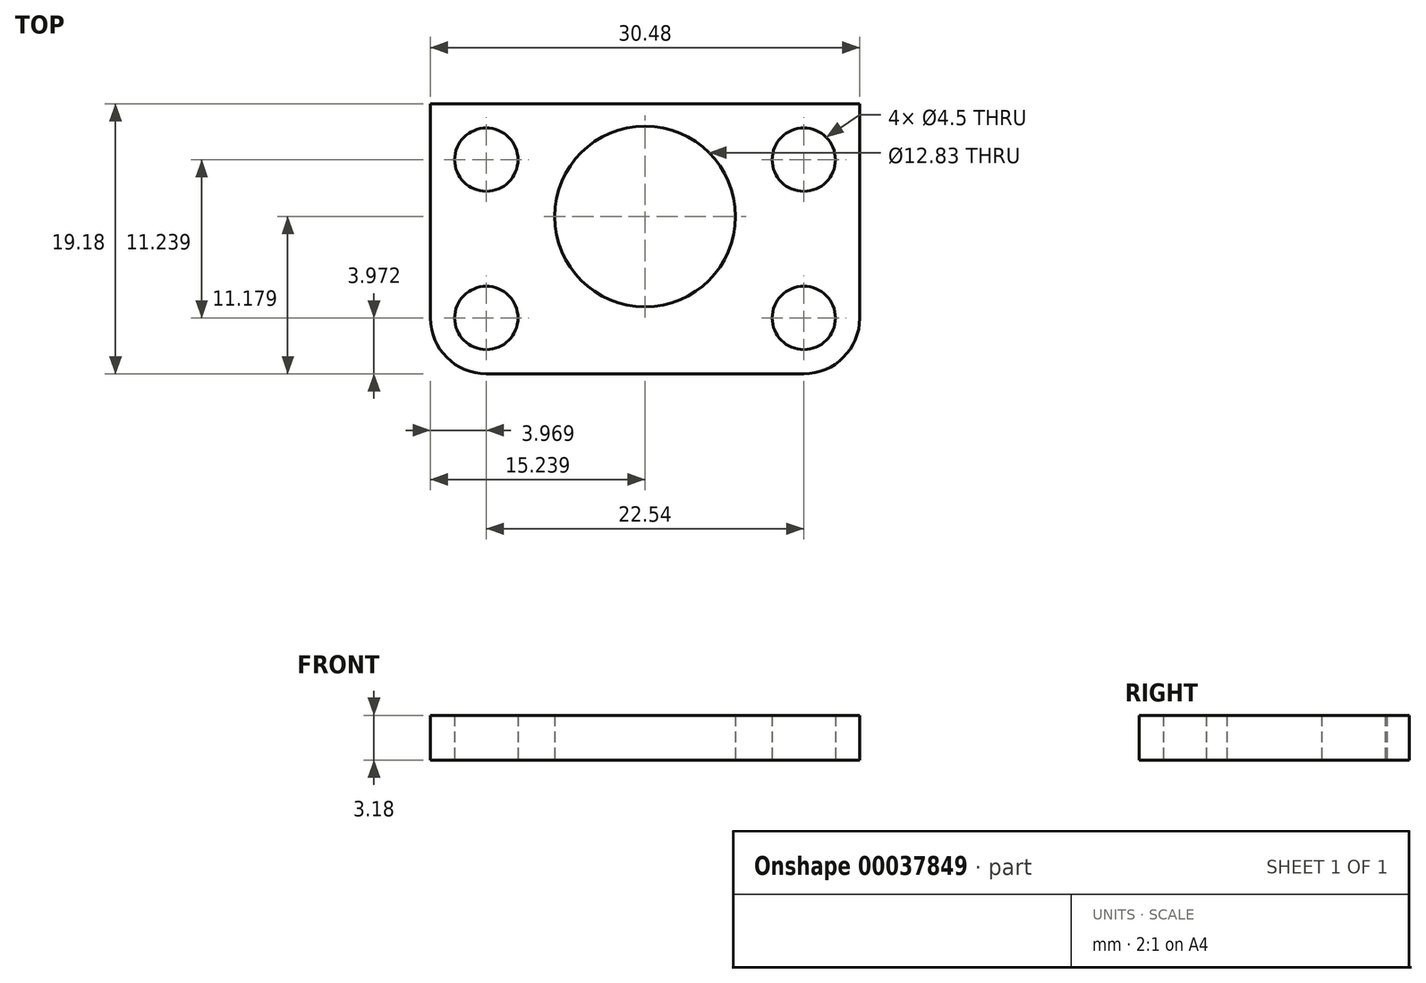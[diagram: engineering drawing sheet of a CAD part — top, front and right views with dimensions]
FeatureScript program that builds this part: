
annotation { "Feature Type Name" : "Feature", "Feature Type Description" : "" }
export const myFeature = defineFeature(function(context is Context, id is Id, definition is map)
    precondition{}
    {
        {
            var Q0;
            Q0=qCreatedBy(makeId("Top.planeOp"),FACE);
            var sketch = newSketch(context, id + "F0", { "sketchPlane" : qUnion([Q0])});
            skLineSegment(sketch, "E0.bottom", {"start": v(0, 0) * mm, "end": v(30.48, 0) * mm});
            skLineSegment(sketch, "E0.top", {"start": v(0, -19.18) * mm, "end": v(30.48, -19.18) * mm});
            skLineSegment(sketch, "E0.left", {"start": v(0, 0) * mm, "end": v(0, -19.18) * mm});
            skLineSegment(sketch, "E0.right", {"start": v(30.48, 0) * mm, "end": v(30.48, -19.18) * mm});
            skLineSegment(sketch, "E1", {"start": v(15.24, 0) * mm, "end": v(15.24, -3.97) * mm, "construction": true});
            skLineSegment(sketch, "E2", {"start": v(15.24, -19.18) * mm, "end": v(15.24, -15.2) * mm, "construction": true});
            skLineSegment(sketch, "E3", {"start": v(3.97, -3.97) * mm, "end": v(26.5, -3.97) * mm, "construction": true});
            skLineSegment(sketch, "E4", {"start": v(3.97, -15.2) * mm, "end": v(26.5, -15.2) * mm, "construction": true});
            skLineSegment(sketch, "E5", {"start": v(26.5, -15.2) * mm, "end": v(30.48, -15.2) * mm, "construction": true});
            skLineSegment(sketch, "E6", {"start": v(15.24, -3.97) * mm, "end": v(15.24, -8) * mm, "construction": true});
            skCircle(sketch, "E7", {"center": v(15.24, -8) * mm, "radius": 6.41 * mm});
            skCircle(sketch, "E8", {"center": v(3.97, -3.97) * mm, "radius": 3.97 * mm, "construction": true});
            skCircle(sketch, "E9", {"center": v(15.24, -8) * mm, "radius": 8 * mm, "construction": true});
            skCircle(sketch, "E10", {"center": v(3.97, -3.97) * mm, "radius": 2.25 * mm});
            skCircle(sketch, "E11", {"center": v(3.97, -15.2) * mm, "radius": 2.25 * mm});
            skCircle(sketch, "E12", {"center": v(26.5, -15.2) * mm, "radius": 2.25 * mm});
            skCircle(sketch, "E13", {"center": v(26.5, -3.97) * mm, "radius": 2.25 * mm});
            skSolve(sketch);
        }
        {
            var Q0;
            Q0 = qSketchRegion(id + "F0", true);
            extrude(context, id + "F1", {"entities" : qUnion([Q0]), "depth" : 3.17 * mm});
        }
        {
            var Q0;
            Q0=makeQuery(id+"F1.opExtrude","SWEPT_EDGE",EDGE,{"disambiguationData":[OSD([sQuery(id+"F0.wireOp",EDGE,"E0.top"),sQuery(id+"F0.wireOp",EDGE,"E0.left")])]});
            var Q1;
            Q1=makeQuery(id+"F1.opExtrude","SWEPT_EDGE",EDGE,{"disambiguationData":[OSD([sQuery(id+"F0.wireOp",EDGE,"E0.top"),sQuery(id+"F0.wireOp",EDGE,"E0.right")])]});
            fillet(context, id + "F2", {"entities" : qUnion([Q0, Q1]), "radius" : 3.97 * mm, "tangentPropagation" : true, "allowEdgeOverflow" : false});
        }
    });
